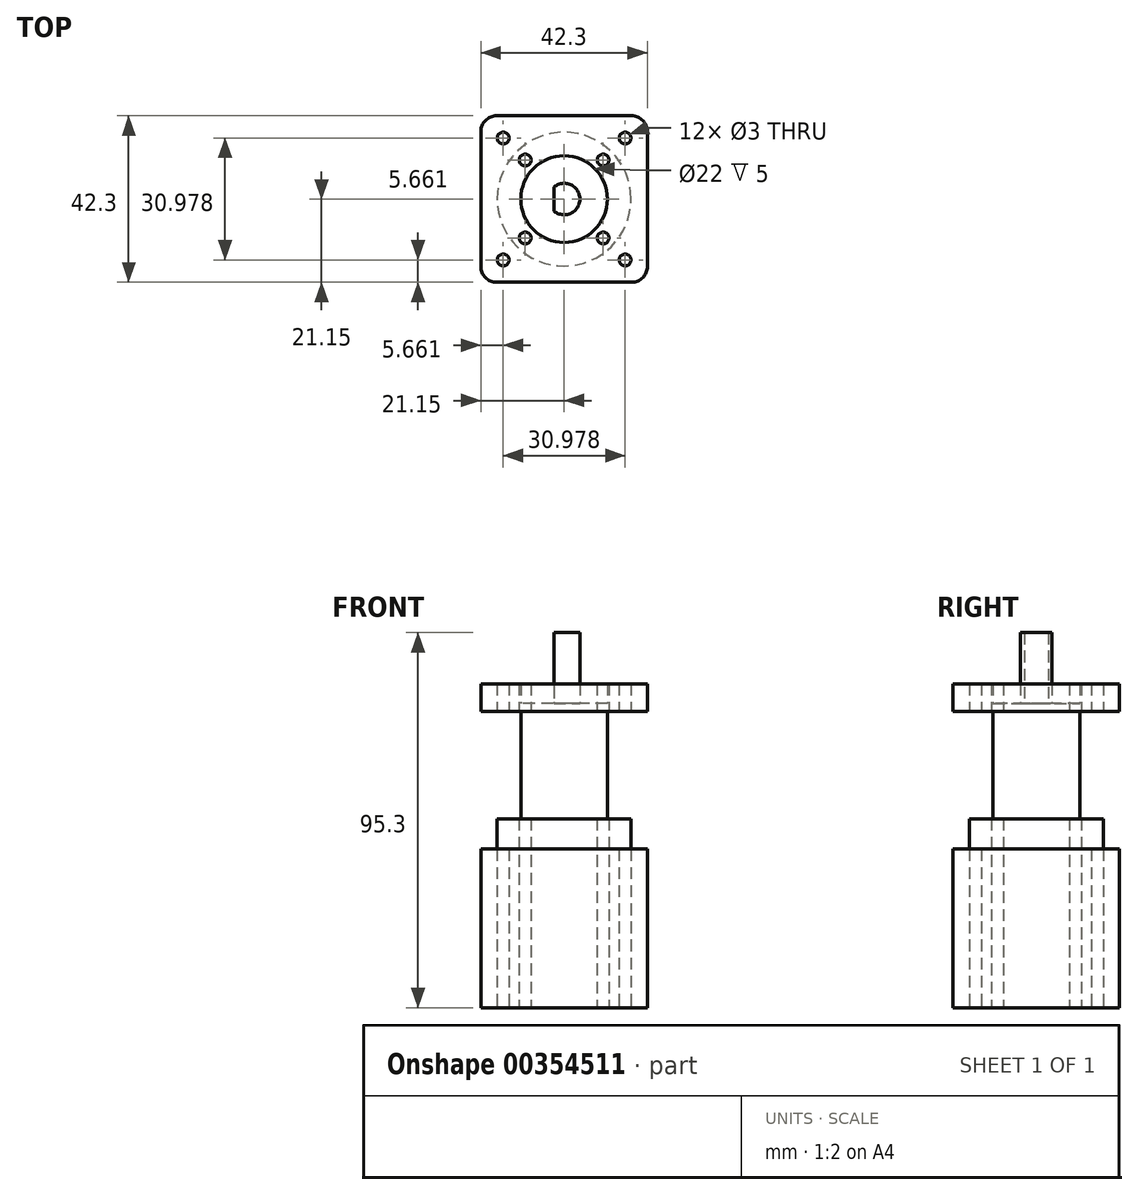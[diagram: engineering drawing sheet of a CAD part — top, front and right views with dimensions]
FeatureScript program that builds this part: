
annotation { "Feature Type Name" : "Feature", "Feature Type Description" : "" }
export const myFeature = defineFeature(function(context is Context, id is Id, definition is map)
    precondition{}
    {
        {
            var Q0;
            Q0=qCreatedBy(makeId("Top.planeOp"),FACE);
            var sketch = newSketch(context, id + "F0", { "sketchPlane" : qUnion([Q0])});
            skCircle(sketch, "E0", {"center": v(0, 0) * mm, "radius": 11 * mm});
            skArc(sketch, "E1", {"start": v(-2.63, -3.02) * mm, "mid": v(4, 0) * mm, "end": v(-2.63, 3.02) * mm});
            skLineSegment(sketch, "E2", {"start": v(-2.63, 3.02) * mm, "end": v(-2.63, -3.02) * mm});
            skLineSegment(sketch, "E3.bottom", {"start": v(-17.15, -21.15) * mm, "end": v(17.15, -21.15) * mm});
            skLineSegment(sketch, "E3.top", {"start": v(-17.15, 21.15) * mm, "end": v(17.15, 21.15) * mm});
            skLineSegment(sketch, "E3.left", {"start": v(-21.15, -17.15) * mm, "end": v(-21.15, 17.15) * mm});
            skLineSegment(sketch, "E3.right", {"start": v(21.15, -17.15) * mm, "end": v(21.15, 17.15) * mm});
            skLineSegment(sketch, "E4", {"start": v(0, 0) * mm, "end": v(31.51, 31.51) * mm, "construction": true});
            skPoint(sketch, "E5.visualSharp", {"position": v(21.15, 21.15) * mm});
            skArc(sketch, "E5.filletArc", {"start": v(21.15, 17.15) * mm, "mid": v(19.98, 19.98) * mm, "end": v(17.15, 21.15) * mm});
            skCircle(sketch, "E6", {"center": v(0, 0) * mm, "radius": 21.9 * mm, "construction": true});
            skCircle(sketch, "E7", {"center": v(0, 0) * mm, "radius": 14 * mm, "construction": true});
            skCircle(sketch, "E8", {"center": v(15.49, 15.49) * mm, "radius": 1.5 * mm});
            skCircle(sketch, "E9", {"center": v(9.9, 9.9) * mm, "radius": 1.5 * mm});
            skCircle(sketch, "E10.MirrorC", {"center": v(9.9, -9.9) * mm, "radius": 1.5 * mm});
            skCircle(sketch, "E11.MirrorC", {"center": v(15.49, -15.49) * mm, "radius": 1.5 * mm});
            skArc(sketch, "E12.MirrorCS", {"start": v(21.15, -17.15) * mm, "mid": v(19.98, -19.98) * mm, "end": v(17.15, -21.15) * mm});
            skArc(sketch, "E13.MirrorCS", {"start": v(-21.15, 17.15) * mm, "mid": v(-19.98, 19.98) * mm, "end": v(-17.15, 21.15) * mm});
            skCircle(sketch, "E14.MirrorC", {"center": v(-15.49, 15.49) * mm, "radius": 1.5 * mm});
            skCircle(sketch, "E15.MirrorC", {"center": v(-9.9, 9.9) * mm, "radius": 1.5 * mm});
            skCircle(sketch, "E16.MirrorC", {"center": v(-9.9, -9.9) * mm, "radius": 1.5 * mm});
            skCircle(sketch, "E17.MirrorC", {"center": v(-15.49, -15.49) * mm, "radius": 1.5 * mm});
            skArc(sketch, "E18.MirrorCS", {"start": v(-21.15, -17.15) * mm, "mid": v(-19.98, -19.98) * mm, "end": v(-17.15, -21.15) * mm});
            skLineSegment(sketch, "E19.MirrorCS", {"start": v(0, 0) * mm, "end": v(-31.51, 31.51) * mm, "construction": true});
            skLineSegment(sketch, "E20.MirrorCS", {"start": v(0, 0) * mm, "end": v(-31.51, -31.51) * mm, "construction": true});
            skLineSegment(sketch, "E21.MirrorCS", {"start": v(0, 0) * mm, "end": v(31.51, -31.51) * mm, "construction": true});
            skPoint(sketch, "E22.orphan", {"position": v(-21.15, 21.15) * mm});
            skPoint(sketch, "E23.orphan", {"position": v(-21.15, -21.15) * mm});
            skPoint(sketch, "E24.orphan", {"position": v(21.15, -21.15) * mm});
            skCircle(sketch, "E25", {"center": v(0, 0) * mm, "radius": 17 * mm});
            skSolve(sketch);
        }
        {
            var Q0;
            Q0=makeQuery(id+"F0.imprint","IMPRINT",FACE,{"disambiguationData":[TD([[makeQuery(id+"F0.imprint","IMPRINT",EDGE,{"derivedFrom":sQuery(id+"F0.wireOp",EDGE,"E3.bottom")}),1.0]])]});
            var Q1;
            Q1=makeQuery(id+"F0.imprint","IMPRINT",FACE,{"disambiguationData":[TD([[makeQuery(id+"F0.imprint","IMPRINT",EDGE,{"derivedFrom":sQuery(id+"F0.wireOp",EDGE,"E0")}),-1.0]])]});
            extrude(context, id + "F1", {"entities" : qUnion([Q0, Q1]), "depth" : 7 * mm});
        }
        {
            var Q0;
            Q0=makeQuery(id+"F0.imprint","IMPRINT",FACE,{"disambiguationData":[TD([[makeQuery(id+"F0.imprint","IMPRINT",EDGE,{"derivedFrom":sQuery(id+"F0.wireOp",EDGE,"E1")}),1.0]])]});
            extrude(context, id + "F2", {"entities" : qUnion([Q0]), "depth" : 20 * mm});
        }
        {
            var Q0;
            Q0=makeQuery(id+"F0.imprint","IMPRINT",FACE,{"disambiguationData":[TD([[makeQuery(id+"F0.imprint","IMPRINT",EDGE,{"derivedFrom":sQuery(id+"F0.wireOp",EDGE,"E0")}),1.0]])]});
            extrude(context, id + "F3", {"entities" : qUnion([Q0]), "operationType" : NewBodyOperationType.ADD, "depth" : 2 * mm});
        }
        {
            var Q0;
            Q0=makeQuery(id+"F0.imprint","IMPRINT",FACE,{"disambiguationData":[TD([[makeQuery(id+"F0.imprint","IMPRINT",EDGE,{"derivedFrom":sQuery(id+"F0.wireOp",EDGE,"E1")}),1.0]])]});
            var Q1;
            Q1=makeQuery(id+"F0.imprint","IMPRINT",FACE,{"disambiguationData":[TD([[makeQuery(id+"F0.imprint","IMPRINT",EDGE,{"derivedFrom":sQuery(id+"F0.wireOp",EDGE,"E8")}),1.0]])]});
            var Q2;
            Q2=makeQuery(id+"F0.imprint","IMPRINT",FACE,{"disambiguationData":[TD([[makeQuery(id+"F0.imprint","IMPRINT",EDGE,{"derivedFrom":sQuery(id+"F0.wireOp",EDGE,"E10.MirrorC")}),-1.0]])]});
            var Q3;
            Q3=makeQuery(id+"F0.imprint","IMPRINT",FACE,{"disambiguationData":[TD([[makeQuery(id+"F0.imprint","IMPRINT",EDGE,{"derivedFrom":sQuery(id+"F0.wireOp",EDGE,"E14.MirrorC")}),-1.0]])]});
            var Q4;
            Q4=makeQuery(id+"F0.imprint","IMPRINT",FACE,{"disambiguationData":[TD([[makeQuery(id+"F0.imprint","IMPRINT",EDGE,{"derivedFrom":sQuery(id+"F0.wireOp",EDGE,"E15.MirrorC")}),-1.0]])]});
            var Q5;
            Q5=makeQuery(id+"F0.imprint","IMPRINT",FACE,{"disambiguationData":[TD([[makeQuery(id+"F0.imprint","IMPRINT",EDGE,{"derivedFrom":sQuery(id+"F0.wireOp",EDGE,"E0")}),1.0]])]});
            var Q6;
            Q6=makeQuery(id+"F0.imprint","IMPRINT",FACE,{"disambiguationData":[TD([[makeQuery(id+"F0.imprint","IMPRINT",EDGE,{"derivedFrom":sQuery(id+"F0.wireOp",EDGE,"E3.bottom")}),1.0]])]});
            var Q7;
            Q7=makeQuery(id+"F0.imprint","IMPRINT",FACE,{"disambiguationData":[TD([[makeQuery(id+"F0.imprint","IMPRINT",EDGE,{"derivedFrom":sQuery(id+"F0.wireOp",EDGE,"E0")}),-1.0]])]});
            var Q8;
            {var subQ0=sQuery(id+"F0.wireOp",EDGE,"E2");var subQ1=sQuery(id+"F0.wireOp",EDGE,"E1");Q8=makeQuery(id+"F3.boolean.opBoolean","MERGE",FACE,{"derivedFrom":[makeQuery(id+"F2.opExtrude","CAP_FACE",FACE,{"disambiguationData":[OSD([subQ1,subQ0])],"isStart":true}),makeQuery(id+"F3.opExtrude","CAP_FACE",FACE,{"disambiguationData":[OSD([sQuery(id+"F0.wireOp",EDGE,"E0"),subQ1,subQ0])],"isStart":true})]});}
            var Q9;
            Q9=makeQuery(id+"F0.imprint","IMPRINT",FACE,{"disambiguationData":[TD([[makeQuery(id+"F0.imprint","IMPRINT",EDGE,{"derivedFrom":sQuery(id+"F0.wireOp",EDGE,"E11.MirrorC")}),-1.0]])]});
            var Q10;
            Q10=makeQuery(id+"F0.imprint","IMPRINT",FACE,{"disambiguationData":[TD([[makeQuery(id+"F0.imprint","IMPRINT",EDGE,{"derivedFrom":sQuery(id+"F0.wireOp",EDGE,"E9")}),1.0]])]});
            var Q11;
            Q11=makeQuery(id+"F0.imprint","IMPRINT",FACE,{"disambiguationData":[TD([[makeQuery(id+"F0.imprint","IMPRINT",EDGE,{"derivedFrom":sQuery(id+"F0.wireOp",EDGE,"E16.MirrorC")}),1.0]])]});
            var Q12;
            Q12=makeQuery(id+"F0.imprint","IMPRINT",FACE,{"disambiguationData":[TD([[makeQuery(id+"F0.imprint","IMPRINT",EDGE,{"derivedFrom":sQuery(id+"F0.wireOp",EDGE,"E17.MirrorC")}),1.0]])]});
            extrude(context, id + "F4", {"entities" : qUnion([Q0, Q1, Q2, Q3, Q4, Q5, Q6, Q7, Q8, Q9, Q10, Q11, Q12]), "operationType" : NewBodyOperationType.ADD, "oppositeDirection" : true, "depth" : 75.3 * mm});
        }
        {
            var Q0;
            Q0=makeQuery(id+"F0.imprint","IMPRINT",FACE,{"disambiguationData":[TD([[makeQuery(id+"F0.imprint","IMPRINT",EDGE,{"derivedFrom":sQuery(id+"F0.wireOp",EDGE,"E11.MirrorC")}),-1.0]])]});
            var Q1;
            Q1=makeQuery(id+"F0.imprint","IMPRINT",FACE,{"disambiguationData":[TD([[makeQuery(id+"F0.imprint","IMPRINT",EDGE,{"derivedFrom":sQuery(id+"F0.wireOp",EDGE,"E8")}),1.0]])]});
            var Q2;
            Q2=makeQuery(id+"F0.imprint","IMPRINT",FACE,{"disambiguationData":[TD([[makeQuery(id+"F0.imprint","IMPRINT",EDGE,{"derivedFrom":sQuery(id+"F0.wireOp",EDGE,"E9")}),1.0]])]});
            var Q3;
            Q3=makeQuery(id+"F0.imprint","IMPRINT",FACE,{"disambiguationData":[TD([[makeQuery(id+"F0.imprint","IMPRINT",EDGE,{"derivedFrom":sQuery(id+"F0.wireOp",EDGE,"E10.MirrorC")}),-1.0]])]});
            var Q4;
            Q4=makeQuery(id+"F0.imprint","IMPRINT",FACE,{"disambiguationData":[TD([[makeQuery(id+"F0.imprint","IMPRINT",EDGE,{"derivedFrom":sQuery(id+"F0.wireOp",EDGE,"E16.MirrorC")}),1.0]])]});
            var Q5;
            Q5=makeQuery(id+"F0.imprint","IMPRINT",FACE,{"disambiguationData":[TD([[makeQuery(id+"F0.imprint","IMPRINT",EDGE,{"derivedFrom":sQuery(id+"F0.wireOp",EDGE,"E15.MirrorC")}),-1.0]])]});
            var Q6;
            Q6=makeQuery(id+"F0.imprint","IMPRINT",FACE,{"disambiguationData":[TD([[makeQuery(id+"F0.imprint","IMPRINT",EDGE,{"derivedFrom":sQuery(id+"F0.wireOp",EDGE,"E14.MirrorC")}),-1.0]])]});
            var Q7;
            Q7=makeQuery(id+"F0.imprint","IMPRINT",FACE,{"disambiguationData":[TD([[makeQuery(id+"F0.imprint","IMPRINT",EDGE,{"derivedFrom":sQuery(id+"F0.wireOp",EDGE,"E17.MirrorC")}),1.0]])]});
            var Q8;
            Q8=makeQuery(id+"F0.imprint","IMPRINT",FACE,{"disambiguationData":[TD([[makeQuery(id+"F0.imprint","IMPRINT",EDGE,{"derivedFrom":sQuery(id+"F0.wireOp",EDGE,"E3.bottom")}),1.0]])]});
            extrude(context, id + "F5", {"entities" : qUnion([Q0, Q1, Q2, Q3, Q4, Q5, Q6, Q7, Q8]), "operationType" : NewBodyOperationType.REMOVE, "oppositeDirection" : true, "depth" : 27.3 * mm});
        }
        {
            var Q0;
            Q0=makeQuery(id+"F0.imprint","IMPRINT",FACE,{"disambiguationData":[TD([[makeQuery(id+"F0.imprint","IMPRINT",EDGE,{"derivedFrom":sQuery(id+"F0.wireOp",EDGE,"E11.MirrorC")}),-1.0]])]});
            var Q1;
            Q1=makeQuery(id+"F0.imprint","IMPRINT",FACE,{"disambiguationData":[TD([[makeQuery(id+"F0.imprint","IMPRINT",EDGE,{"derivedFrom":sQuery(id+"F0.wireOp",EDGE,"E14.MirrorC")}),-1.0]])]});
            var Q2;
            Q2=makeQuery(id+"F0.imprint","IMPRINT",FACE,{"disambiguationData":[TD([[makeQuery(id+"F0.imprint","IMPRINT",EDGE,{"derivedFrom":sQuery(id+"F0.wireOp",EDGE,"E8")}),1.0]])]});
            var Q3;
            Q3=makeQuery(id+"F0.imprint","IMPRINT",FACE,{"disambiguationData":[TD([[makeQuery(id+"F0.imprint","IMPRINT",EDGE,{"derivedFrom":sQuery(id+"F0.wireOp",EDGE,"E17.MirrorC")}),1.0]])]});
            extrude(context, id + "F6", {"entities" : qUnion([Q0, Q1, Q2, Q3]), "operationType" : NewBodyOperationType.REMOVE, "oppositeDirection" : true, "depth" : 35 * mm});
        }
    });
